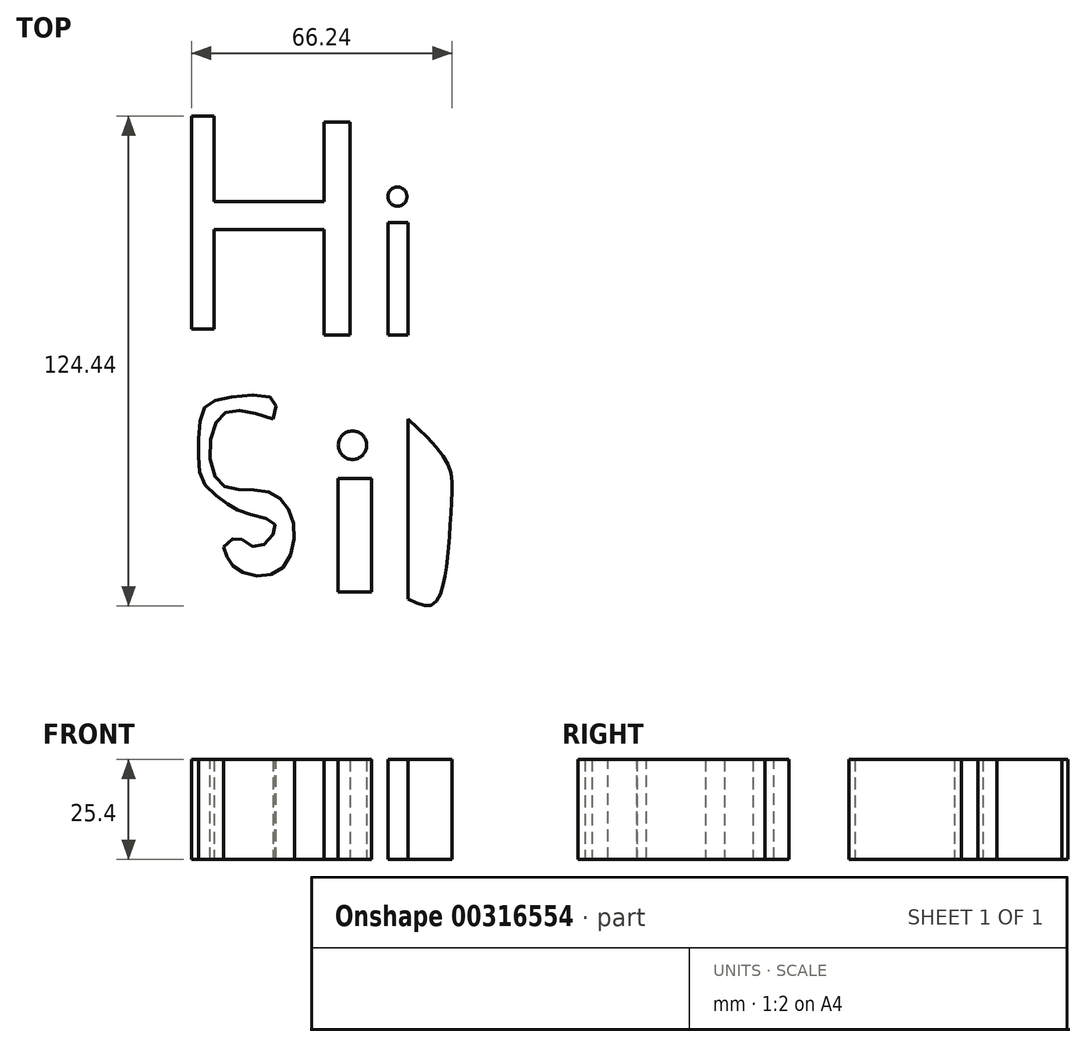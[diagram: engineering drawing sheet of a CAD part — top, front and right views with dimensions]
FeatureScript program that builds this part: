
annotation { "Feature Type Name" : "Feature", "Feature Type Description" : "" }
export const myFeature = defineFeature(function(context is Context, id is Id, definition is map)
    precondition{}
    {
        {
            var Q0;
            Q0=qCreatedBy(makeId("Top.planeOp"),FACE);
            var sketch = newSketch(context, id + "F0", { "sketchPlane" : qUnion([Q0])});
            skLineSegment(sketch, "E0.bottom", {"start": v(-70.69, 66.17) * mm, "end": v(-64.97, 66.17) * mm});
            skLineSegment(sketch, "E0.top", {"start": v(-70.69, 12.03) * mm, "end": v(-64.97, 12.03) * mm});
            skLineSegment(sketch, "E0.left", {"start": v(-70.69, 66.17) * mm, "end": v(-70.69, 12.03) * mm});
            skLineSegment(sketch, "E0.right", {"start": v(-64.97, 66.17) * mm, "end": v(-64.97, 12.03) * mm});
            skLineSegment(sketch, "E1.bottom", {"start": v(-64.97, 44.52) * mm, "end": v(-37, 44.52) * mm});
            skLineSegment(sketch, "E1.top", {"start": v(-64.97, 37.3) * mm, "end": v(-37, 37.3) * mm});
            skLineSegment(sketch, "E1.left", {"start": v(-64.97, 44.52) * mm, "end": v(-64.97, 37.3) * mm});
            skLineSegment(sketch, "E1.right", {"start": v(-37, 44.52) * mm, "end": v(-37, 37.3) * mm});
            skLineSegment(sketch, "E2.bottom", {"start": v(-37, 64.67) * mm, "end": v(-30.38, 64.67) * mm});
            skLineSegment(sketch, "E2.top", {"start": v(-37, 10.53) * mm, "end": v(-30.38, 10.53) * mm});
            skLineSegment(sketch, "E2.left", {"start": v(-37, 64.67) * mm, "end": v(-37, 10.53) * mm});
            skLineSegment(sketch, "E2.right", {"start": v(-30.38, 64.67) * mm, "end": v(-30.38, 10.53) * mm});
            skSolve(sketch);
        }
        {
            var Q0;
            Q0 = qSketchRegion(id + "F0", true);
            extrude(context, id + "F1", {"entities" : qUnion([Q0]), "depth" : 25.4 * mm});
        }
        {
            var Q0;
            Q0=qCreatedBy(makeId("Top.planeOp"),FACE);
            var sketch = newSketch(context, id + "F2", { "sketchPlane" : qUnion([Q0])});
            skLineSegment(sketch, "E3.bottom", {"start": v(-20.75, 39.1) * mm, "end": v(-15.64, 39.1) * mm});
            skLineSegment(sketch, "E3.top", {"start": v(-20.75, 10.53) * mm, "end": v(-15.64, 10.53) * mm});
            skLineSegment(sketch, "E3.left", {"start": v(-20.75, 39.1) * mm, "end": v(-20.75, 10.53) * mm});
            skLineSegment(sketch, "E3.right", {"start": v(-15.64, 39.1) * mm, "end": v(-15.64, 10.53) * mm});
            skCircle(sketch, "E4", {"center": v(-18.35, 45.72) * mm, "radius": 2.4 * mm});
            skFitSpline(sketch, "E5", {"points": [v(-49.93, -10.83) * mm, v(-63.47, -10.23) * mm, v(-63.77, -26.77) * mm, v(-51.74, -29.18) * mm, v(-44.82, -37) * mm, v(-48.43, -49.33) * mm, v(-58.95, -49.03) * mm, v(-62.56, -43.31) * mm], "startDerivative": vector(-103.54, 36.47) * mm, "endDerivative": vector(-20.38, 59.31) * mm});
            skFitSpline(sketch, "E6", {"points": [v(-62.56, -43.31) * mm, v(-58.95, -40.9) * mm, v(-54.44, -43.31) * mm, v(-49.93, -40) * mm, v(-49.93, -37) * mm, v(-57.15, -34.6) * mm, v(-61.83, -32.18) * mm, v(-67.68, -26.77) * mm, v(-68.88, -18.65) * mm, v(-67.68, -8.42) * mm, v(-61.83, -5.41) * mm, v(-49.93, -5.72) * mm, v(-49.93, -10.83) * mm], "startDerivative": vector(51.72, 57.78) * mm, "endDerivative": vector(-24.51, -82.34) * mm});
            skLineSegment(sketch, "E7.bottom", {"start": v(-33.39, -25.87) * mm, "end": v(-24.97, -25.87) * mm});
            skLineSegment(sketch, "E7.top", {"start": v(-33.39, -54.74) * mm, "end": v(-24.97, -54.74) * mm});
            skLineSegment(sketch, "E7.left", {"start": v(-33.39, -25.87) * mm, "end": v(-33.39, -54.74) * mm});
            skLineSegment(sketch, "E7.right", {"start": v(-24.97, -25.87) * mm, "end": v(-24.97, -54.74) * mm});
            skPoint(sketch, "E7.middle", {"position": v(-29.18, -40.3) * mm});
            skCircle(sketch, "E8", {"center": v(-29.78, -17.45) * mm, "radius": 3.6 * mm});
            skLineSegment(sketch, "E9", {"start": v(-15.64, -10.83) * mm, "end": v(-15.64, -56.55) * mm});
            skFitSpline(sketch, "E10", {"points": [v(-15.64, -10.83) * mm, v(-5.71, -21.96) * mm, v(-4.51, -30.38) * mm, v(-5.41, -43.31) * mm, v(-6.62, -52.34) * mm, v(-9.63, -58.05) * mm, v(-15.64, -56.55) * mm], "startDerivative": vector(58.43, -54.26) * mm, "endDerivative": vector(-49.6, 24.35) * mm});
            skSolve(sketch);
        }
        {
            var Q0;
            Q0 = qSketchRegion(id + "F2", true);
            extrude(context, id + "F3", {"entities" : qUnion([Q0]), "depth" : 25.4 * mm});
        }
    });
